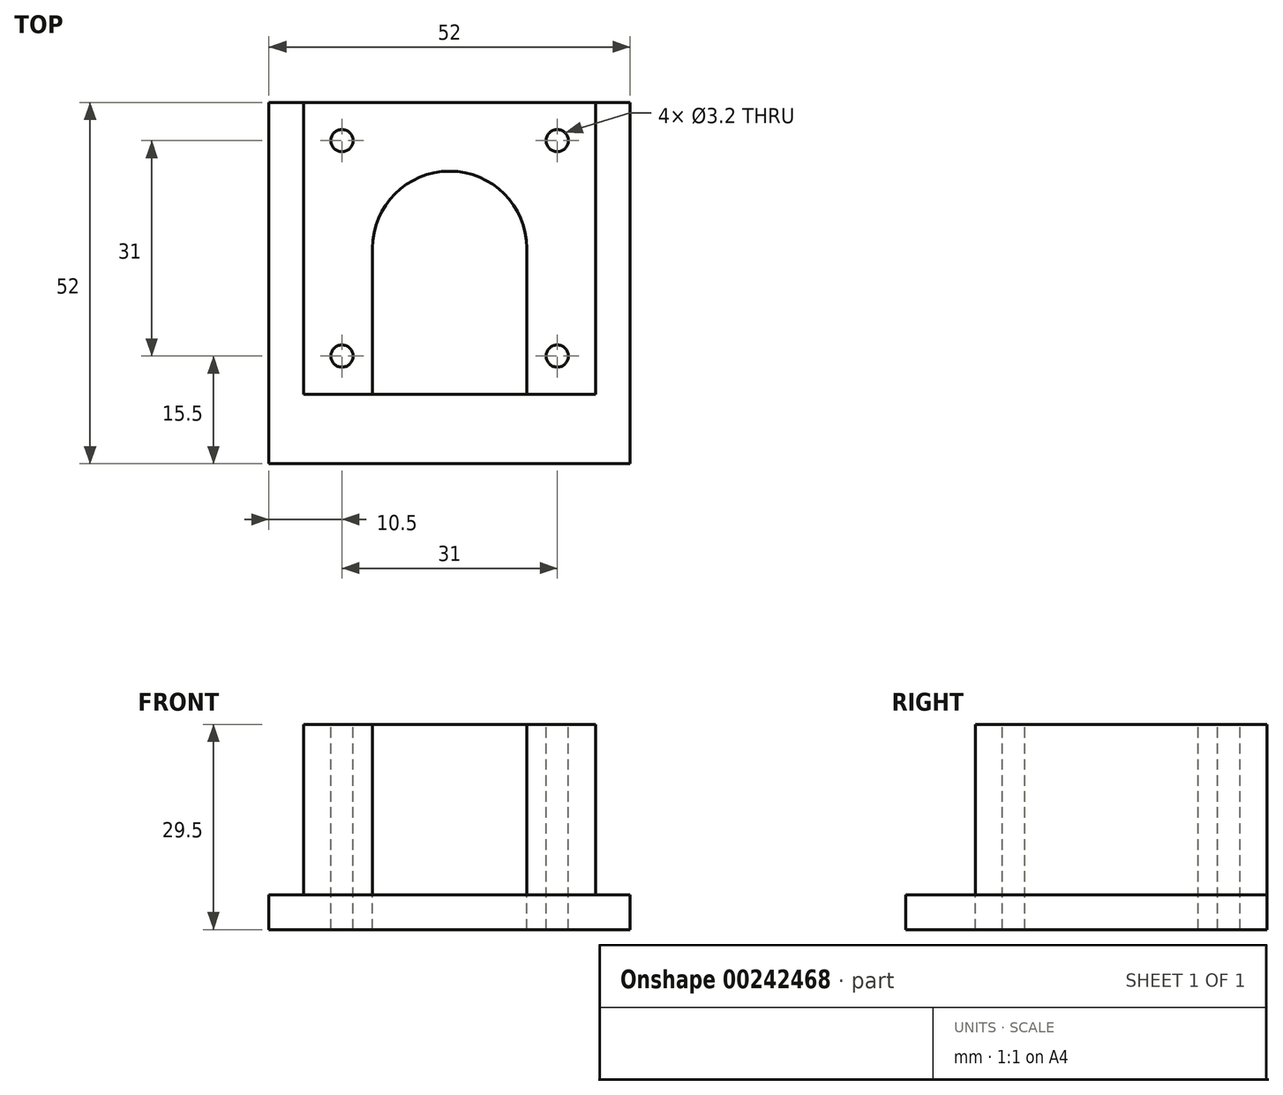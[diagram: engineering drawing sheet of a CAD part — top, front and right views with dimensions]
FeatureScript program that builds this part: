
annotation { "Feature Type Name" : "Feature", "Feature Type Description" : "" }
export const myFeature = defineFeature(function(context is Context, id is Id, definition is map)
    precondition{}
    {
        {
            var Q0;
            Q0=qCreatedBy(makeId("Top.planeOp"),FACE);
            var sketch = newSketch(context, id + "F0", { "sketchPlane" : qUnion([Q0])});
            skLineSegment(sketch, "E0.bottom", {"start": v(26, -26) * mm, "end": v(-26, -26) * mm});
            skLineSegment(sketch, "E0.top", {"start": v(26, 26) * mm, "end": v(-26, 26) * mm});
            skLineSegment(sketch, "E0.left", {"start": v(26, -26) * mm, "end": v(26, 26) * mm});
            skLineSegment(sketch, "E0.right", {"start": v(-26, -26) * mm, "end": v(-26, 26) * mm});
            skPoint(sketch, "E0.middle", {"position": v(0, 0) * mm});
            skSolve(sketch);
        }
        {
            var Q0;
            Q0=makeQuery(id+"F0.imprint","IMPRINT",FACE,{"disambiguationData":[TD([[makeQuery(id+"F0.imprint","IMPRINT",EDGE,{"derivedFrom":sQuery(id+"F0.wireOp",EDGE,"E0.bottom")}),-1.0]])]});
            extrude(context, id + "F1", {"entities" : qUnion([Q0]), "depth" : 5 * mm});
        }
        {
            var Q0;
            Q0=makeQuery(id+"F1.opExtrude","CAP_FACE",FACE,{"disambiguationData":[OSD([sQuery(id+"F0.wireOp",EDGE,"E0.bottom"),sQuery(id+"F0.wireOp",EDGE,"E0.top"),sQuery(id+"F0.wireOp",EDGE,"E0.left"),sQuery(id+"F0.wireOp",EDGE,"E0.right")])],"isStart":false});
            var sketch = newSketch(context, id + "F2", { "sketchPlane" : qUnion([Q0])});
            skLineSegment(sketch, "E1.bottom", {"start": v(21, -16) * mm, "end": v(-21, -16) * mm});
            skLineSegment(sketch, "E1.top", {"start": v(21, 26) * mm, "end": v(-21, 26) * mm});
            skLineSegment(sketch, "E1.left", {"start": v(21, -16) * mm, "end": v(21, 26) * mm});
            skLineSegment(sketch, "E1.right", {"start": v(-21, -16) * mm, "end": v(-21, 26) * mm});
            skPoint(sketch, "E1.middle", {"position": v(0, 5) * mm});
            skPoint(sketch, "E2", {"position": v(0, 26) * mm});
            skSolve(sketch);
        }
        {
            var Q0;
            Q0=makeQuery(id+"F2.imprint","IMPRINT",FACE,{"disambiguationData":[TD([[makeQuery(id+"F2.imprint","IMPRINT",EDGE,{"derivedFrom":sQuery(id+"F2.wireOp",EDGE,"E1.bottom")}),-1.0]])]});
            extrude(context, id + "F3", {"entities" : qUnion([Q0]), "operationType" : NewBodyOperationType.ADD, "depth" : 24.5 * mm});
        }
        {
            var Q0;
            Q0=makeQuery(id+"F3.opExtrude","CAP_FACE",FACE,{"disambiguationData":[OSD([sQuery(id+"F2.wireOp",EDGE,"E1.bottom"),sQuery(id+"F2.wireOp",EDGE,"E1.top"),sQuery(id+"F2.wireOp",EDGE,"E1.left"),sQuery(id+"F2.wireOp",EDGE,"E1.right")])],"isStart":false});
            var sketch = newSketch(context, id + "F4", { "sketchPlane" : qUnion([Q0])});
            skLineSegment(sketch, "E3.bottom", {"start": v(15.5, -10.5) * mm, "end": v(-15.5, -10.5) * mm, "construction": true});
            skLineSegment(sketch, "E3.top", {"start": v(15.5, 20.5) * mm, "end": v(-15.5, 20.5) * mm, "construction": true});
            skLineSegment(sketch, "E3.left", {"start": v(15.5, -10.5) * mm, "end": v(15.5, 20.5) * mm, "construction": true});
            skLineSegment(sketch, "E3.right", {"start": v(-15.5, -10.5) * mm, "end": v(-15.5, 20.5) * mm, "construction": true});
            skCircle(sketch, "E4", {"center": v(-15.5, 20.5) * mm, "radius": 1.6 * mm});
            skCircle(sketch, "E5", {"center": v(15.5, 20.5) * mm, "radius": 1.6 * mm});
            skCircle(sketch, "E6", {"center": v(-15.5, -10.5) * mm, "radius": 1.6 * mm});
            skCircle(sketch, "E7", {"center": v(15.5, -10.5) * mm, "radius": 1.6 * mm});
            skCircle(sketch, "E8", {"center": v(0, 5) * mm, "radius": 11.1 * mm});
            skLineSegment(sketch, "E9", {"start": v(-15.5, 20.5) * mm, "end": v(15.5, -10.5) * mm, "construction": true});
            skLineSegment(sketch, "E10", {"start": v(15.5, 20.5) * mm, "end": v(-15.5, -10.5) * mm, "construction": true});
            skLineSegment(sketch, "E11", {"start": v(11.1, 5) * mm, "end": v(11.1, -16) * mm});
            skLineSegment(sketch, "E12", {"start": v(-11.1, 5) * mm, "end": v(-11.1, -16) * mm});
            skLineSegment(sketch, "E13", {"start": v(-21, 26) * mm, "end": v(21, -16) * mm, "construction": true});
            skLineSegment(sketch, "E14", {"start": v(21, 26) * mm, "end": v(-21, -16) * mm, "construction": true});
            skSolve(sketch);
        }
        {
            var Q0;
            Q0=qSketchRegion(id+"F4",true);
            var Q1;
            {var subQ0=sQuery(id+"F4.wireOp",EDGE,"JUiuH9Jo-Xia1-40vq-F6NH-Q2W5IGgyVVrA");Q1=makeQuery(id+"F4.imprint","IMPRINT",FACE,{"disambiguationData":[TD([[makeQuery(id+"F4.imprint","IMPRINT",EDGE,{"derivedFrom":subQ0}),1.0]])]});}
            var Q2;
            {var subQ0=sQuery(id+"F4.wireOp",EDGE,"E11");Q2=makeQuery(id+"F4.imprint","IMPRINT",FACE,{"disambiguationData":[TD([[makeQuery(id+"F4.imprint","IMPRINT",EDGE,{"derivedFrom":subQ0}),-1.0]])]});}
            var Q3;
            Q3=makeQuery(id+"F1.opExtrude","CAP_FACE",FACE,{"disambiguationData":[OSD([sQuery(id+"F0.wireOp",EDGE,"E0.bottom"),sQuery(id+"F0.wireOp",EDGE,"E0.top"),sQuery(id+"F0.wireOp",EDGE,"E0.left"),sQuery(id+"F0.wireOp",EDGE,"E0.right")])],"isStart":true});
            extrude(context, id + "F5", {"entities" : qUnion([Q0, Q1, Q2]), "operationType" : NewBodyOperationType.REMOVE, "endBound" : BoundingType.UP_TO_SURFACE, "oppositeDirection" : true, "endBoundEntityFace" : qUnion([Q3]), "depth" : 25 * mm});
        }
    });
